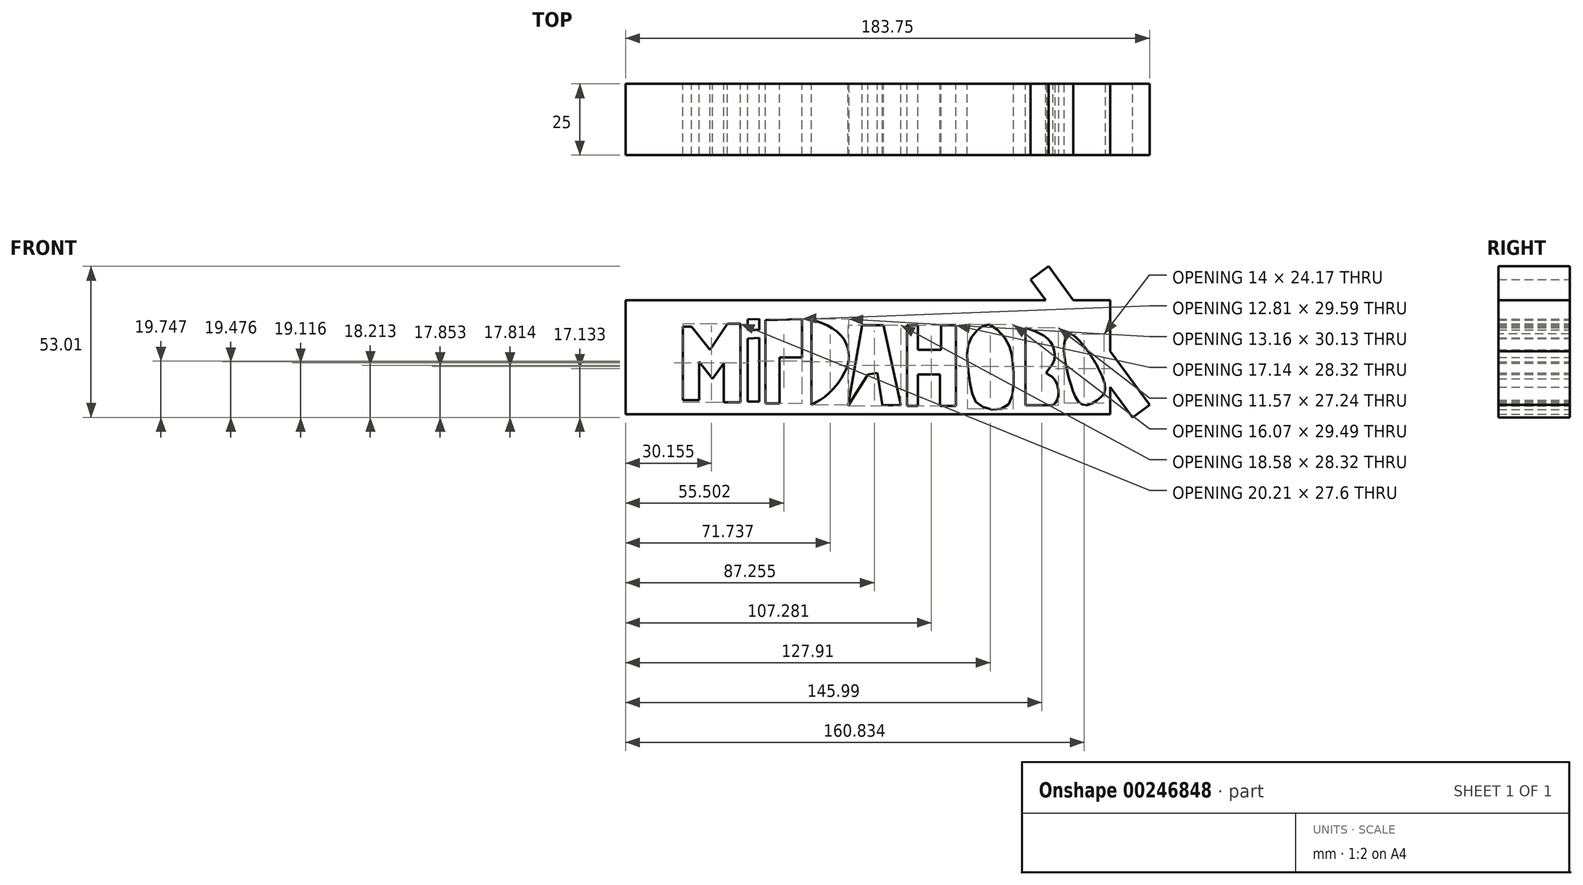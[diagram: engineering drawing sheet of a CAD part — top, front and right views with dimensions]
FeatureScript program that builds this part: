
annotation { "Feature Type Name" : "Feature", "Feature Type Description" : "" }
export const myFeature = defineFeature(function(context is Context, id is Id, definition is map)
    precondition{}
    {
        {
            var Q0;
            Q0=qCreatedBy(makeId("Front.planeOp"),FACE);
            var sketch = newSketch(context, id + "F0", { "sketchPlane" : qUnion([Q0])});
            skLineSegment(sketch, "E0.bottom", {"start": v(-85, 20) * mm, "end": v(85, 20) * mm});
            skLineSegment(sketch, "E0.top", {"start": v(-85, -20) * mm, "end": v(85, -20) * mm});
            skLineSegment(sketch, "E0.left", {"start": v(-85, 20) * mm, "end": v(-85, -20) * mm});
            skLineSegment(sketch, "E0.right", {"start": v(85, 20) * mm, "end": v(85, -20) * mm});
            skPoint(sketch, "E0.middle", {"position": v(0, 0) * mm});
            skLineSegment(sketch, "E1", {"start": v(-64.95, -15.06) * mm, "end": v(-64.95, 10.73) * mm});
            skLineSegment(sketch, "E2", {"start": v(-64.95, 10.73) * mm, "end": v(-61.88, 10.73) * mm});
            skLineSegment(sketch, "E3", {"start": v(-64.95, -15.06) * mm, "end": v(-59.18, -15.06) * mm});
            skLineSegment(sketch, "E4", {"start": v(-59.18, -15.06) * mm, "end": v(-59.18, -1.53) * mm});
            skLineSegment(sketch, "E5", {"start": v(-59.18, -1.53) * mm, "end": v(-54.48, -7.49) * mm});
            skLineSegment(sketch, "E6", {"start": v(-54.48, -7.49) * mm, "end": v(-50.52, -2.07) * mm});
            skPoint(sketch, "E7.end.orphan", {"position": v(-46.9, -7.49) * mm});
            skLineSegment(sketch, "E8", {"start": v(-50.52, -2.07) * mm, "end": v(-50.52, -15.79) * mm});
            skLineSegment(sketch, "E9", {"start": v(-50.52, -15.79) * mm, "end": v(-44.74, -15.79) * mm});
            skLineSegment(sketch, "E10", {"start": v(-44.74, -15.79) * mm, "end": v(-44.74, 11.82) * mm});
            skLineSegment(sketch, "E11", {"start": v(-44.74, 11.82) * mm, "end": v(-49.25, 11.82) * mm});
            skLineSegment(sketch, "E12", {"start": v(-49.25, 11.82) * mm, "end": v(-55.39, 2.62) * mm});
            skLineSegment(sketch, "E13", {"start": v(-55.39, 2.62) * mm, "end": v(-61.88, 10.73) * mm});
            skLineSegment(sketch, "E14", {"start": v(-42.22, 6.59) * mm, "end": v(-42.22, -15.6) * mm});
            skLineSegment(sketch, "E15", {"start": v(-42.22, -15.6) * mm, "end": v(-38.07, -15.6) * mm});
            skLineSegment(sketch, "E16", {"start": v(-38.07, -15.6) * mm, "end": v(-38.07, 6.77) * mm});
            skLineSegment(sketch, "E17", {"start": v(-38.07, 6.77) * mm, "end": v(-42.22, 6.59) * mm});
            skLineSegment(sketch, "E18", {"start": v(-42.22, 13.26) * mm, "end": v(-42.22, 9.65) * mm});
            skLineSegment(sketch, "E19", {"start": v(-42.22, 9.65) * mm, "end": v(-38.07, 9.65) * mm});
            skLineSegment(sketch, "E20", {"start": v(-38.07, 9.65) * mm, "end": v(-38.07, 13.44) * mm});
            skLineSegment(sketch, "E21", {"start": v(-38.07, 13.44) * mm, "end": v(-42.22, 13.26) * mm});
            skLineSegment(sketch, "E22", {"start": v(-35.9, 13.08) * mm, "end": v(-35.9, -16.15) * mm});
            skLineSegment(sketch, "E23", {"start": v(-35.9, -16.15) * mm, "end": v(-31.03, -16.15) * mm});
            skLineSegment(sketch, "E24", {"start": v(-31.03, -16.15) * mm, "end": v(-31.03, 0) * mm});
            skLineSegment(sketch, "E25", {"start": v(-31.03, 0) * mm, "end": v(-23.1, 0) * mm});
            skLineSegment(sketch, "E26", {"start": v(-23.1, 0) * mm, "end": v(-23.1, 13.44) * mm});
            skLineSegment(sketch, "E27", {"start": v(-23.1, 13.44) * mm, "end": v(-35.9, 13.08) * mm});
            skLineSegment(sketch, "E28", {"start": v(-19.85, 13.44) * mm, "end": v(-19.85, -16.69) * mm});
            skPoint(sketch, "E29.2.internal.snap0", {"position": v(-38.07, -4.42) * mm});
            skFitSpline(sketch, "E29", {"points": [v(-19.85, -16.69) * mm, v(-13.53, -12.54) * mm, v(-7.76, -4.42) * mm, v(-6.68, 0) * mm, v(-7.76, 5.14) * mm, v(-11.9, 9.83) * mm, v(-19.85, 13.44) * mm], "startDerivative": vector(36.71, 18.86) * mm, "endDerivative": vector(-45.88, 16.9) * mm});
            skLineSegment(sketch, "E30", {"start": v(-7.04, -17.05) * mm, "end": v(-1.98, 11.28) * mm});
            skLineSegment(sketch, "E31", {"start": v(-1.98, 11.28) * mm, "end": v(5.41, 11.28) * mm});
            skLineSegment(sketch, "E32", {"start": v(5.41, 11.28) * mm, "end": v(11.55, -16.87) * mm});
            skLineSegment(sketch, "E33", {"start": v(11.55, -16.87) * mm, "end": v(5.05, -16.87) * mm});
            skLineSegment(sketch, "E34", {"start": v(5.05, -16.87) * mm, "end": v(3.25, -5.5) * mm});
            skLineSegment(sketch, "E35", {"start": v(3.25, -5.5) * mm, "end": v(0, -6.02) * mm});
            skLineSegment(sketch, "E36", {"start": v(0, -6.02) * mm, "end": v(-7.04, -17.05) * mm});
            skLineSegment(sketch, "E37", {"start": v(13.71, 11.28) * mm, "end": v(13.71, -17.05) * mm});
            skLineSegment(sketch, "E38", {"start": v(13.71, -17.05) * mm, "end": v(17.5, -17.05) * mm});
            skLineSegment(sketch, "E39", {"start": v(17.5, -17.05) * mm, "end": v(17.5, -6.02) * mm});
            skLineSegment(sketch, "E40", {"start": v(17.5, -6.02) * mm, "end": v(25.26, -6.02) * mm});
            skLineSegment(sketch, "E41", {"start": v(25.26, -6.02) * mm, "end": v(25.26, -17.05) * mm});
            skLineSegment(sketch, "E42", {"start": v(25.26, -17.05) * mm, "end": v(30.85, -17.05) * mm});
            skLineSegment(sketch, "E43", {"start": v(30.85, -17.05) * mm, "end": v(30.85, 11.28) * mm});
            skLineSegment(sketch, "E44", {"start": v(30.85, 11.28) * mm, "end": v(25.62, 11.28) * mm});
            skLineSegment(sketch, "E45", {"start": v(25.62, 11.28) * mm, "end": v(25.62, 2.62) * mm});
            skLineSegment(sketch, "E46", {"start": v(25.62, 2.62) * mm, "end": v(17.5, 2.62) * mm});
            skLineSegment(sketch, "E47", {"start": v(17.5, 2.62) * mm, "end": v(17.5, 11.28) * mm});
            skLineSegment(sketch, "E48", {"start": v(17.5, 11.28) * mm, "end": v(13.71, 11.28) * mm});
            skLineSegment(sketch, "E49", {"start": v(55.2, 10.37) * mm, "end": v(55.2, -16.87) * mm});
            skLineSegment(sketch, "E50", {"start": v(55.2, -16.87) * mm, "end": v(64.95, -16.87) * mm});
            skFitSpline(sketch, "E51", {"points": [v(64.95, -16.87) * mm, v(66.75, -13.8) * mm, v(64.95, -7.13) * mm, v(62.6, -5.5) * mm, v(64.95, -2.07) * mm, v(64.95, 3.7) * mm, v(61.52, 7.67) * mm, v(55.2, 10.37) * mm], "startDerivative": vector(19.2, 20.08) * mm, "endDerivative": vector(-40.4, 13.88) * mm});
            skFitSpline(sketch, "E52", {"points": [v(70.72, 8.2) * mm, v(68.74, 3.34) * mm, v(69.46, -2.62) * mm, v(71.26, -10.01) * mm, v(75.41, -16.69) * mm, v(81.55, -14.16) * mm, v(82.8, -8.39) * mm, v(70.72, 8.2) * mm]});
            skLineSegment(sketch, "E53", {"start": v(63.36, 31.91) * mm, "end": v(57.01, 27.2) * mm});
            skLineSegment(sketch, "E54", {"start": v(57.01, 27.2) * mm, "end": v(92.9, -21.1) * mm});
            skLineSegment(sketch, "E55", {"start": v(92.9, -21.1) * mm, "end": v(98.75, -16.75) * mm});
            skLineSegment(sketch, "E56", {"start": v(98.75, -16.75) * mm, "end": v(63.36, 31.91) * mm});
            skFitSpline(sketch, "E57", {"points": [v(42.58, 11.46) * mm, v(39.15, 10.2) * mm, v(35.72, 5.86) * mm, v(34.82, 0) * mm, v(35.72, -8.39) * mm, v(37.89, -15.6) * mm, v(43.66, -18.31) * mm, v(49.43, -16.33) * mm, v(51.06, -7.49) * mm, v(50.52, 0) * mm, v(48.71, 5.68) * mm, v(42.58, 11.46) * mm]});
            skSolve(sketch);
        }
        {
            var Q0;
            Q0 = qSketchRegion(id + "F0", true);
            extrude(context, id + "F1", {"entities" : qUnion([Q0]), "depth" : 25 * mm});
        }
    });
